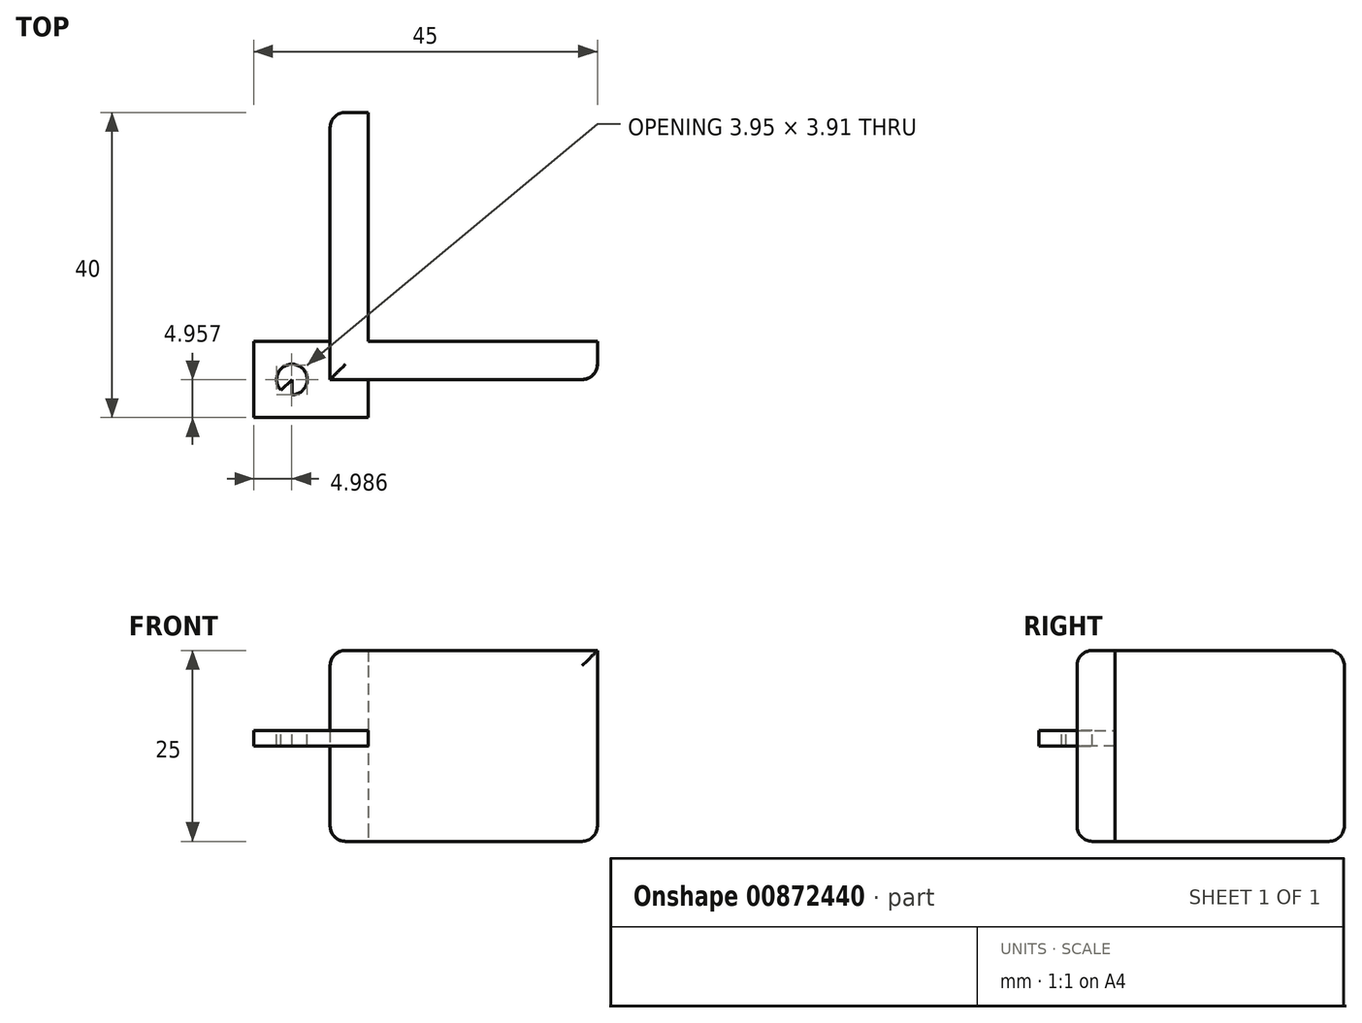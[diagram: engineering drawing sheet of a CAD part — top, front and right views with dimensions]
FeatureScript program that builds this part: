
annotation { "Feature Type Name" : "Feature", "Feature Type Description" : "" }
export const myFeature = defineFeature(function(context is Context, id is Id, definition is map)
    precondition{}
    {
        {
            var Q0;
            Q0=qCreatedBy(makeId("Top.planeOp"),FACE);
            var sketch = newSketch(context, id + "F0", { "sketchPlane" : qUnion([Q0])});
            skLineSegment(sketch, "E0", {"start": v(0, 0) * mm, "end": v(-30, 0) * mm});
            skLineSegment(sketch, "E1", {"start": v(-30, 0) * mm, "end": v(-30, 30) * mm});
            skLineSegment(sketch, "E2", {"start": v(-30, 30) * mm, "end": v(-35, 30) * mm});
            skLineSegment(sketch, "E3", {"start": v(-35, 30) * mm, "end": v(-35, -5) * mm});
            skLineSegment(sketch, "E4", {"start": v(-35, -5) * mm, "end": v(0, -5) * mm});
            skLineSegment(sketch, "E5", {"start": v(0, -5) * mm, "end": v(0, 0) * mm});
            skSolve(sketch);
        }
        {
            var Q0;
            Q0 = qSketchRegion(id + "F0", true);
            extrude(context, id + "F1", {"entities" : qUnion([Q0]), "depth" : 25 * mm, "offsetDistance" : 25 * mm});
        }
        {
            var Q0;
            Q0=makeQuery(id+"F1.opExtrude","SWEPT_FACE",FACE,{"disambiguationData":[OSD([sQuery(id+"F0.wireOp",EDGE,"E4")])]});
            var sketch = newSketch(context, id + "F2", { "sketchPlane" : qUnion([Q0])});
            skLineSegment(sketch, "E6", {"start": v(-35, 12.5) * mm, "end": v(0, 12.5) * mm});
            skLineSegment(sketch, "E7", {"start": v(-35, 12.5) * mm, "end": v(-35, 14.5) * mm});
            skLineSegment(sketch, "E8", {"start": v(-35, 14.5) * mm, "end": v(-30, 14.5) * mm});
            skLineSegment(sketch, "E9", {"start": v(-30, 14.5) * mm, "end": v(-30, 12.5) * mm});
            skSolve(sketch);
        }
        {
            var Q0;
            {var subQ0=sQuery(id+"F2.wireOp",EDGE,"E7");Q0=makeQuery(id+"F2.imprint","IMPRINT",FACE,{"disambiguationData":[TD([[makeQuery(id+"F2.imprint","IMPRINT",EDGE,{"derivedFrom":subQ0}),1.0]])]});}
            extrude(context, id + "F3", {"entities" : qUnion([Q0]), "operationType" : NewBodyOperationType.ADD, "depth" : 5 * mm, "offsetDistance" : 25 * mm});
        }
        {
            var Q0;
            Q0=makeQuery(id+"F3.boolean.opBoolean","MERGE",FACE,{"derivedFrom":[makeQuery(id+"F1.opExtrude","SWEPT_FACE",FACE,{"disambiguationData":[OSD([sQuery(id+"F0.wireOp",EDGE,"E3")])]}),makeQuery(id+"F3.opExtrude","SWEPT_FACE",FACE,{"disambiguationData":[OSD([sQuery(id+"F2.wireOp",EDGE,"E7")])]})]});
            var sketch = newSketch(context, id + "F4", { "sketchPlane" : qUnion([Q0])});
            skLineSegment(sketch, "E10", {"start": v(5, 14.5) * mm, "end": v(0, 14.5) * mm});
            skLineSegment(sketch, "E11", {"start": v(0, 14.5) * mm, "end": v(0, 12.5) * mm});
            skLineSegment(sketch, "E12", {"start": v(0, 12.5) * mm, "end": v(10, 12.5) * mm});
            skLineSegment(sketch, "E13", {"start": v(10, 12.5) * mm, "end": v(10, 14.5) * mm});
            skSolve(sketch);
        }
        {
            var Q0;
            Q0 = qSketchRegion(id + "F4", true);
            var Q1;
            Q1=makeQuery(id+"F4.imprint","IMPRINT",FACE,{"disambiguationData":[TD([[makeQuery(id+"F4.imprint","IMPRINT",EDGE,{"derivedFrom":sQuery(id+"F4.wireOp",EDGE,"E10")}),1.0]])]});
            extrude(context, id + "F5", {"entities" : qUnion([Q0, Q1]), "operationType" : NewBodyOperationType.ADD, "depth" : 10 * mm, "offsetDistance" : 25 * mm});
        }
        {
            var Q0;
            {var subQ0=sQuery(id+"F2.wireOp",EDGE,"E8");Q0=makeQuery(id+"F5.boolean.opBoolean","MERGE",FACE,{"derivedFrom":[makeQuery(id+"F3.opExtrude","SWEPT_FACE",FACE,{"disambiguationData":[OSD([subQ0])]}),makeQuery(id+"F5.opExtrude","SWEPT_FACE",FACE,{"disambiguationData":[OSD([sQuery(id+"F0.wireOp",EDGE,"E3"),sQuery(id+"F0.wireOp",EDGE,"E4"),sQuery(id+"F2.wireOp",EDGE,"E7"),subQ0,sQuery(id+"F4.wireOp",EDGE,"E10")])]})]});}
            var sketch = newSketch(context, id + "F6", { "sketchPlane" : qUnion([Q0])});
            skLineSegment(sketch, "E14", {"start": v(-35, -5) * mm, "end": v(-45, -5) * mm});
            skLineSegment(sketch, "E15", {"start": v(-45, -5) * mm, "end": v(-45, -10) * mm});
            skLineSegment(sketch, "E16", {"start": v(-45, -10) * mm, "end": v(-40, -10) * mm});
            skLineSegment(sketch, "E17", {"start": v(-40, -10) * mm, "end": v(-40, 0) * mm});
            skLineSegment(sketch, "E18", {"start": v(-40, -5) * mm, "end": v(-45, -10) * mm});
            skCircle(sketch, "E19", {"center": v(-40, -5) * mm, "radius": 2 * mm});
            skSolve(sketch);
        }
        {
            var Q0;
            {var subQ1=sQuery(id+"F6.wireOp",EDGE,"E17");var subQ3=sQuery(id+"F6.wireOp",EDGE,"E19");var subQ4=makeQuery(id+"F6.imprint","INTERSECT",VERTEX,{"disambiguationData":[OD(0.0)],"derivedFrom":[subQ1,subQ3]});Q0=makeQuery(id+"F6.imprint","IMPRINT",FACE,{"disambiguationData":[TD([[makeQuery(id+"F6.imprint","IMPRINT",EDGE,{"disambiguationData":[TD([[subQ4,1.0]])],"derivedFrom":subQ3}),1.0]])]});}
            var Q1;
            {var subQ1=sQuery(id+"F6.wireOp",EDGE,"E14");var subQ3=sQuery(id+"F6.wireOp",EDGE,"E19");var subQ4=makeQuery(id+"F6.imprint","INTERSECT",VERTEX,{"disambiguationData":[OD(0.0)],"derivedFrom":[subQ1,subQ3]});Q1=makeQuery(id+"F6.imprint","IMPRINT",FACE,{"disambiguationData":[TD([[makeQuery(id+"F6.imprint","IMPRINT",EDGE,{"disambiguationData":[TD([[subQ4,1.0]])],"derivedFrom":subQ3}),1.0]])]});}
            var Q2;
            {var subQ1=sQuery(id+"F6.wireOp",EDGE,"E14");var subQ3=sQuery(id+"F6.wireOp",EDGE,"E19");var subQ4=makeQuery(id+"F6.imprint","INTERSECT",VERTEX,{"disambiguationData":[OD(0.0)],"derivedFrom":[subQ1,subQ3]});Q2=makeQuery(id+"F6.imprint","IMPRINT",FACE,{"disambiguationData":[TD([[makeQuery(id+"F6.imprint","IMPRINT",EDGE,{"disambiguationData":[TD([[subQ4,-1.0]])],"derivedFrom":subQ3}),1.0]])]});}
            var Q3;
            {var subQ1=sQuery(id+"F6.wireOp",EDGE,"E14");var subQ3=sQuery(id+"F6.wireOp",EDGE,"E19");var subQ4=makeQuery(id+"F6.imprint","INTERSECT",VERTEX,{"disambiguationData":[OD(1.0)],"derivedFrom":[subQ1,subQ3]});Q3=makeQuery(id+"F6.imprint","IMPRINT",FACE,{"disambiguationData":[TD([[makeQuery(id+"F6.imprint","IMPRINT",EDGE,{"disambiguationData":[TD([[subQ4,1.0]])],"derivedFrom":subQ3}),1.0]])]});}
            var Q4;
            {var subQ1=sQuery(id+"F6.wireOp",EDGE,"E14");var subQ3=sQuery(id+"F6.wireOp",EDGE,"E19");var subQ4=makeQuery(id+"F6.imprint","INTERSECT",VERTEX,{"disambiguationData":[OD(1.0)],"derivedFrom":[subQ1,subQ3]});Q4=makeQuery(id+"F6.imprint","IMPRINT",FACE,{"disambiguationData":[TD([[makeQuery(id+"F6.imprint","IMPRINT",EDGE,{"disambiguationData":[TD([[subQ4,-1.0]])],"derivedFrom":subQ3}),1.0]])]});}
            extrude(context, id + "F7", {"entities" : qUnion([Q0, Q1, Q2, Q3, Q4]), "operationType" : NewBodyOperationType.REMOVE, "oppositeDirection" : true, "depth" : 25 * mm, "offsetDistance" : 25 * mm});
        }
        {
            var Q0;
            Q0=makeQuery(id+"F1.opExtrude","CAP_EDGE",EDGE,{"disambiguationData":[OSD([sQuery(id+"F0.wireOp",EDGE,"E3")])],"isStart":true});
            var Q1;
            Q1=makeQuery(id+"F1.opExtrude","CAP_EDGE",EDGE,{"disambiguationData":[OSD([sQuery(id+"F0.wireOp",EDGE,"E4")])],"isStart":true});
            var Q2;
            Q2=makeQuery(id+"F1.opExtrude","CAP_EDGE",EDGE,{"disambiguationData":[OSD([sQuery(id+"F0.wireOp",EDGE,"E5")])],"isStart":true});
            var Q3;
            Q3=makeQuery(id+"F1.opExtrude","CAP_EDGE",EDGE,{"disambiguationData":[OSD([sQuery(id+"F0.wireOp",EDGE,"E2")])],"isStart":true});
            var Q4;
            Q4=makeQuery(id+"F1.opExtrude","SWEPT_EDGE",EDGE,{"disambiguationData":[OSD([sQuery(id+"F0.wireOp",EDGE,"E2"),sQuery(id+"F0.wireOp",EDGE,"E3")])]});
            var Q5;
            Q5=makeQuery(id+"F1.opExtrude","CAP_EDGE",EDGE,{"disambiguationData":[OSD([sQuery(id+"F0.wireOp",EDGE,"E3")])],"isStart":false});
            var Q6;
            Q6=makeQuery(id+"F1.opExtrude","CAP_EDGE",EDGE,{"disambiguationData":[OSD([sQuery(id+"F0.wireOp",EDGE,"E2")])],"isStart":false});
            var Q7;
            Q7=makeQuery(id+"F1.opExtrude","CAP_EDGE",EDGE,{"disambiguationData":[OSD([sQuery(id+"F0.wireOp",EDGE,"E4")])],"isStart":false});
            var Q8;
            Q8=makeQuery(id+"F1.opExtrude","SWEPT_EDGE",EDGE,{"disambiguationData":[OSD([sQuery(id+"F0.wireOp",EDGE,"E4"),sQuery(id+"F0.wireOp",EDGE,"E5")])]});
            fillet(context, id + "F8", {"entities" : qUnion([Q0, Q1, Q2, Q3, Q4, Q5, Q6, Q7, Q8]), "radius" : 2 * mm, "tangentPropagation" : true, "allowEdgeOverflow" : false});
        }
    });
